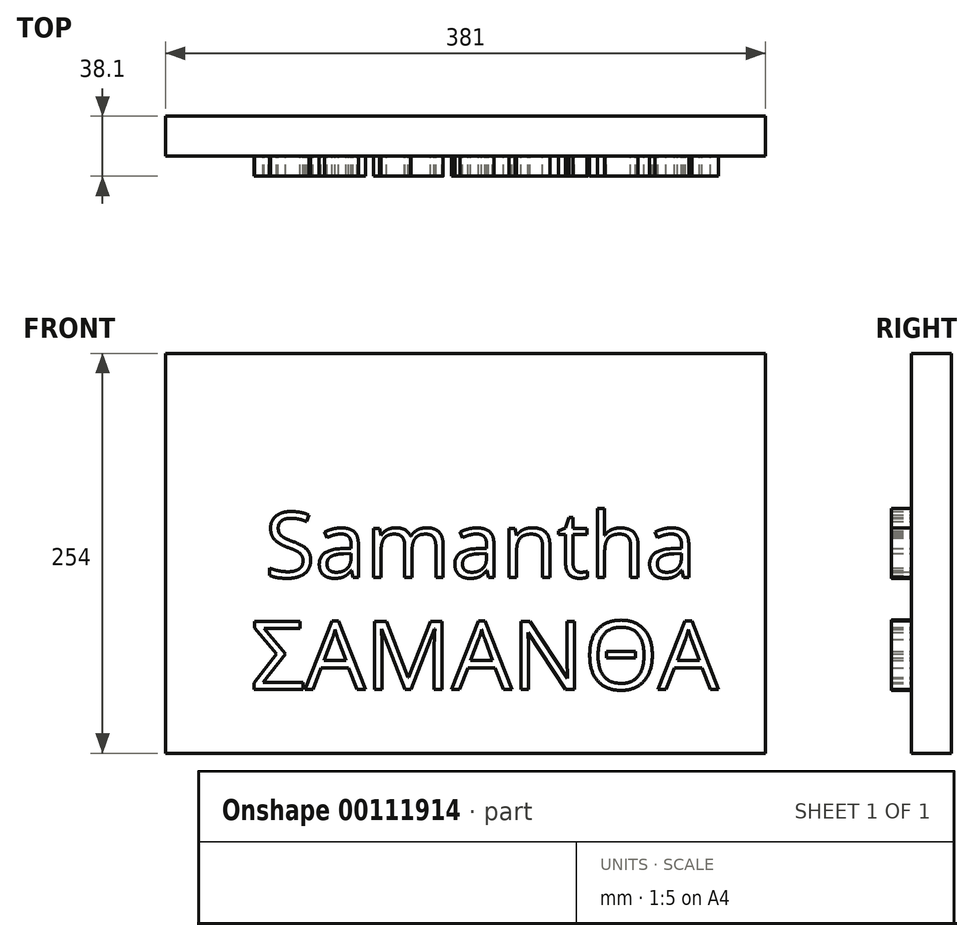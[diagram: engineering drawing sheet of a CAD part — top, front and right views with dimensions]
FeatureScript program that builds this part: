
annotation { "Feature Type Name" : "Feature", "Feature Type Description" : "" }
export const myFeature = defineFeature(function(context is Context, id is Id, definition is map)
    precondition{}
    {
        {
            var Q0;
            Q0=qCreatedBy(makeId("Front.planeOp"),FACE);
            var sketch = newSketch(context, id + "F0", { "sketchPlane" : qUnion([Q0])});
            skLineSegment(sketch, "E0.bottom", {"start": v(190.5, 127) * mm, "end": v(-190.5, 127) * mm});
            skLineSegment(sketch, "E0.top", {"start": v(190.5, -127) * mm, "end": v(-190.5, -127) * mm});
            skLineSegment(sketch, "E0.left", {"start": v(190.5, 127) * mm, "end": v(190.5, -127) * mm});
            skLineSegment(sketch, "E0.right", {"start": v(-190.5, 127) * mm, "end": v(-190.5, -127) * mm});
            skPoint(sketch, "E0.middle", {"position": v(0, 0) * mm});
            skSolve(sketch);
        }
        {
            var Q0;
            Q0 = qSketchRegion(id + "F0", true);
            extrude(context, id + "F1", {"entities" : qUnion([Q0]), "depth" : 25.4 * mm});
        }
        {
            var Q0;
            Q0=makeQuery(id+"F1.opExtrude","CAP_FACE",FACE,{"disambiguationData":[OSD([sQuery(id+"F0.wireOp",EDGE,"E0.bottom"),sQuery(id+"F0.wireOp",EDGE,"E0.top"),sQuery(id+"F0.wireOp",EDGE,"E0.left"),sQuery(id+"F0.wireOp",EDGE,"E0.right")])],"isStart":false});
            var sketch = newSketch(context, id + "F2", { "sketchPlane" : qUnion([Q0])});
            skText(sketch, "E1", { "text": "Samantha", "fontName": "OpenSans-Regular.ttf"});
            const initialGuessF2  = {"E1": [-0.12736, -0.01537, 1, 0, 0.0417]};
            skSetInitialGuess(sketch, initialGuessF2);
            skSolve(sketch);
        }
        {
            var Q0;
            Q0=makeQuery(id+"F2.imprint","IMPRINT",FACE,{"disambiguationData":[TD([[makeQuery(id+"F2.imprint","IMPRINT",EDGE,{"derivedFrom":sQuery(id+"F2.wireOp",EDGE,"E1.sketch_text.stroke-0")}),-1.0]])]});
            var Q1;
            Q1=makeQuery(id+"F2.imprint","IMPRINT",FACE,{"disambiguationData":[TD([[makeQuery(id+"F2.imprint","IMPRINT",EDGE,{"derivedFrom":sQuery(id+"F2.wireOp",EDGE,"E1.sketch_text.stroke-25")}),-1.0]])]});
            var Q2;
            Q2=makeQuery(id+"F2.imprint","IMPRINT",FACE,{"disambiguationData":[TD([[makeQuery(id+"F2.imprint","IMPRINT",EDGE,{"derivedFrom":sQuery(id+"F2.wireOp",EDGE,"E1.sketch_text.stroke-52")}),-1.0]])]});
            var Q3;
            Q3=makeQuery(id+"F2.imprint","IMPRINT",FACE,{"disambiguationData":[TD([[makeQuery(id+"F2.imprint","IMPRINT",EDGE,{"derivedFrom":sQuery(id+"F2.wireOp",EDGE,"E1.sketch_text.stroke-80")}),-1.0]])]});
            var Q4;
            Q4=makeQuery(id+"F2.imprint","IMPRINT",FACE,{"disambiguationData":[TD([[makeQuery(id+"F2.imprint","IMPRINT",EDGE,{"derivedFrom":sQuery(id+"F2.wireOp",EDGE,"E1.sketch_text.stroke-107")}),-1.0]])]});
            var Q5;
            Q5=makeQuery(id+"F2.imprint","IMPRINT",FACE,{"disambiguationData":[TD([[makeQuery(id+"F2.imprint","IMPRINT",EDGE,{"derivedFrom":sQuery(id+"F2.wireOp",EDGE,"E1.sketch_text.stroke-124")}),-1.0]])]});
            var Q6;
            Q6=makeQuery(id+"F2.imprint","IMPRINT",FACE,{"disambiguationData":[TD([[makeQuery(id+"F2.imprint","IMPRINT",EDGE,{"derivedFrom":sQuery(id+"F2.wireOp",EDGE,"E1.sketch_text.stroke-143")}),-1.0]])]});
            var Q7;
            Q7=makeQuery(id+"F2.imprint","IMPRINT",FACE,{"disambiguationData":[TD([[makeQuery(id+"F2.imprint","IMPRINT",EDGE,{"derivedFrom":sQuery(id+"F2.wireOp",EDGE,"E1.sketch_text.stroke-161")}),-1.0]])]});
            extrude(context, id + "F5", {"entities" : qUnion([Q0, Q1, Q2, Q3, Q4, Q5, Q6, Q7]), "operationType" : NewBodyOperationType.ADD, "depth" : 12.7 * mm});
        }
        {
            var Q0;
            {var subQ0=sQuery(id+"F0.wireOp",EDGE,"E0.left");var subQ1=sQuery(id+"F0.wireOp",EDGE,"E0.bottom");var subQ2=sQuery(id+"F0.wireOp",EDGE,"E0.right");var subQ3=sQuery(id+"F0.wireOp",EDGE,"E0.top");Q0=makeQuery(id+"F5.boolean.opBoolean","SPLIT",FACE,{"disambiguationData":[TD([makeQuery(id+"F1.opExtrude","SWEPT_FACE",FACE,{"disambiguationData":[OSD([subQ1])]})])],"derivedFrom":makeQuery(id+"F1.opExtrude","CAP_FACE",FACE,{"disambiguationData":[OSD([subQ1,subQ3,subQ0,subQ2])],"isStart":false})});}
            var sketch = newSketch(context, id + "F3", { "sketchPlane" : qUnion([Q0])});
            skText(sketch, "E2", { "text": "ΣΑΜΑΝΘΑ", "fontName": "OpenSans-Regular.ttf"});
            const initialGuessF3  = {"E2": [-0.13639, -0.08644, 1, 0, 0.04365]};
            skSetInitialGuess(sketch, initialGuessF3);
            skSolve(sketch);
        }
        {
            var Q0;
            Q0=makeQuery(id+"F3.imprint","IMPRINT",FACE,{"disambiguationData":[TD([[makeQuery(id+"F3.imprint","IMPRINT",EDGE,{"derivedFrom":sQuery(id+"F3.wireOp",EDGE,"E2.sketch_text.stroke-0")}),-1.0]])]});
            var Q1;
            Q1=makeQuery(id+"F3.imprint","IMPRINT",FACE,{"disambiguationData":[TD([[makeQuery(id+"F3.imprint","IMPRINT",EDGE,{"derivedFrom":sQuery(id+"F3.wireOp",EDGE,"E2.sketch_text.stroke-13")}),-1.0]])]});
            var Q2;
            Q2=makeQuery(id+"F3.imprint","IMPRINT",FACE,{"disambiguationData":[TD([[makeQuery(id+"F3.imprint","IMPRINT",EDGE,{"derivedFrom":sQuery(id+"F3.wireOp",EDGE,"E2.sketch_text.stroke-26")}),-1.0]])]});
            var Q3;
            Q3=makeQuery(id+"F3.imprint","IMPRINT",FACE,{"disambiguationData":[TD([[makeQuery(id+"F3.imprint","IMPRINT",EDGE,{"derivedFrom":sQuery(id+"F3.wireOp",EDGE,"E2.sketch_text.stroke-44")}),-1.0]])]});
            var Q4;
            Q4=makeQuery(id+"F3.imprint","IMPRINT",FACE,{"disambiguationData":[TD([[makeQuery(id+"F3.imprint","IMPRINT",EDGE,{"derivedFrom":sQuery(id+"F3.wireOp",EDGE,"E2.sketch_text.stroke-57")}),-1.0]])]});
            var Q5;
            Q5=makeQuery(id+"F3.imprint","IMPRINT",FACE,{"disambiguationData":[TD([[makeQuery(id+"F3.imprint","IMPRINT",EDGE,{"derivedFrom":sQuery(id+"F3.wireOp",EDGE,"E2.sketch_text.stroke-72")}),-1.0]])]});
            var Q6;
            Q6=makeQuery(id+"F3.imprint","IMPRINT",FACE,{"disambiguationData":[TD([[makeQuery(id+"F3.imprint","IMPRINT",EDGE,{"derivedFrom":sQuery(id+"F3.wireOp",EDGE,"E2.sketch_text.stroke-76")}),-1.0]])]});
            var Q7;
            Q7=makeQuery(id+"F3.imprint","IMPRINT",FACE,{"disambiguationData":[TD([[makeQuery(id+"F3.imprint","IMPRINT",EDGE,{"derivedFrom":sQuery(id+"F3.wireOp",EDGE,"E2.sketch_text.stroke-92")}),-1.0]])]});
            extrude(context, id + "F4", {"entities" : qUnion([Q0, Q1, Q2, Q3, Q4, Q5, Q6, Q7]), "operationType" : NewBodyOperationType.ADD, "depth" : 12.7 * mm});
        }
    });
